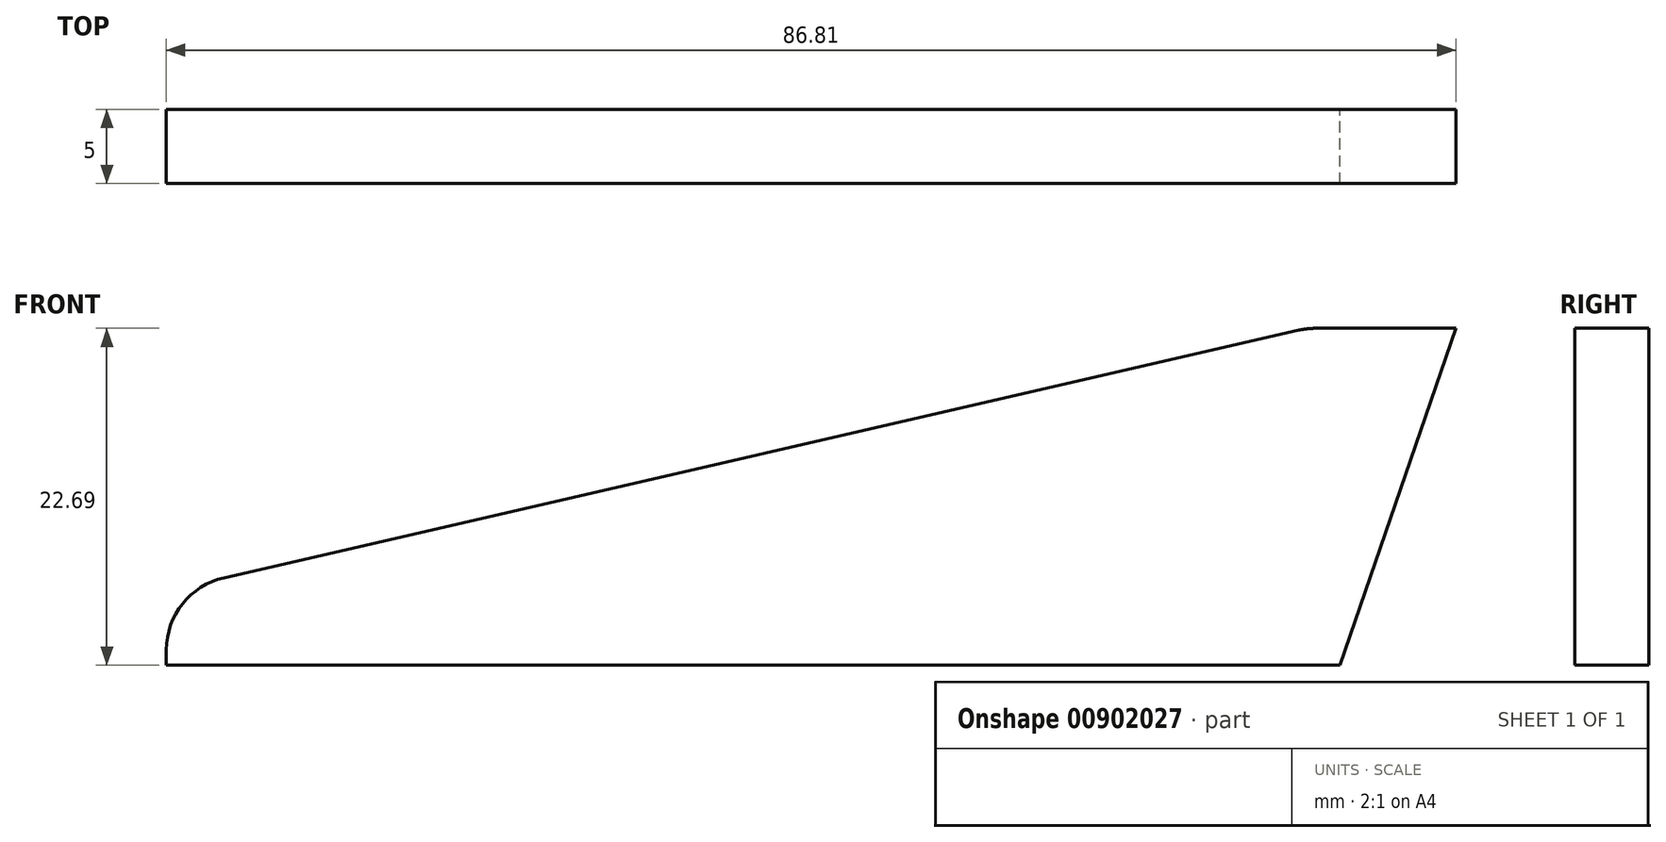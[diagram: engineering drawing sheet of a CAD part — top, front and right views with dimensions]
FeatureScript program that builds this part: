
annotation { "Feature Type Name" : "Feature", "Feature Type Description" : "" }
export const myFeature = defineFeature(function(context is Context, id is Id, definition is map)
    precondition{}
    {
        {
            var Q0;
            Q0=qCreatedBy(makeId("Front.planeOp"),FACE);
            var sketch = newSketch(context, id + "F0", { "sketchPlane" : qUnion([Q0])});
            skLineSegment(sketch, "E0", {"start": v(-79, 0) * mm, "end": v(0, 0) * mm});
            skLineSegment(sketch, "E1", {"start": v(0, 0) * mm, "end": v(7.81, 22.7) * mm});
            skLineSegment(sketch, "E2", {"start": v(7.81, 22.7) * mm, "end": v(-1.62, 22.7) * mm});
            skLineSegment(sketch, "E3", {"start": v(-2.74, 22.56) * mm, "end": v(-75.12, 5.9) * mm});
            skLineSegment(sketch, "E4", {"start": v(-79, 1.02) * mm, "end": v(-79, 0) * mm});
            skPoint(sketch, "E5.visualSharp", {"position": v(-79, 5) * mm});
            skArc(sketch, "E5.filletArc", {"start": v(-75.12, 5.9) * mm, "mid": v(-77.91, 4.13) * mm, "end": v(-79, 1.02) * mm});
            skPoint(sketch, "E6.visualSharp", {"position": v(-2.19, 22.7) * mm});
            skArc(sketch, "E6.filletArc", {"start": v(-1.62, 22.7) * mm, "mid": v(-2.18, 22.66) * mm, "end": v(-2.74, 22.56) * mm});
            skSolve(sketch);
        }
        {
            var Q0;
            Q0 = qSketchRegion(id + "F0", true);
            extrude(context, id + "F1", {"entities" : qUnion([Q0]), "depth" : 5 * mm, "offsetDistance" : 25 * mm});
        }
    });
